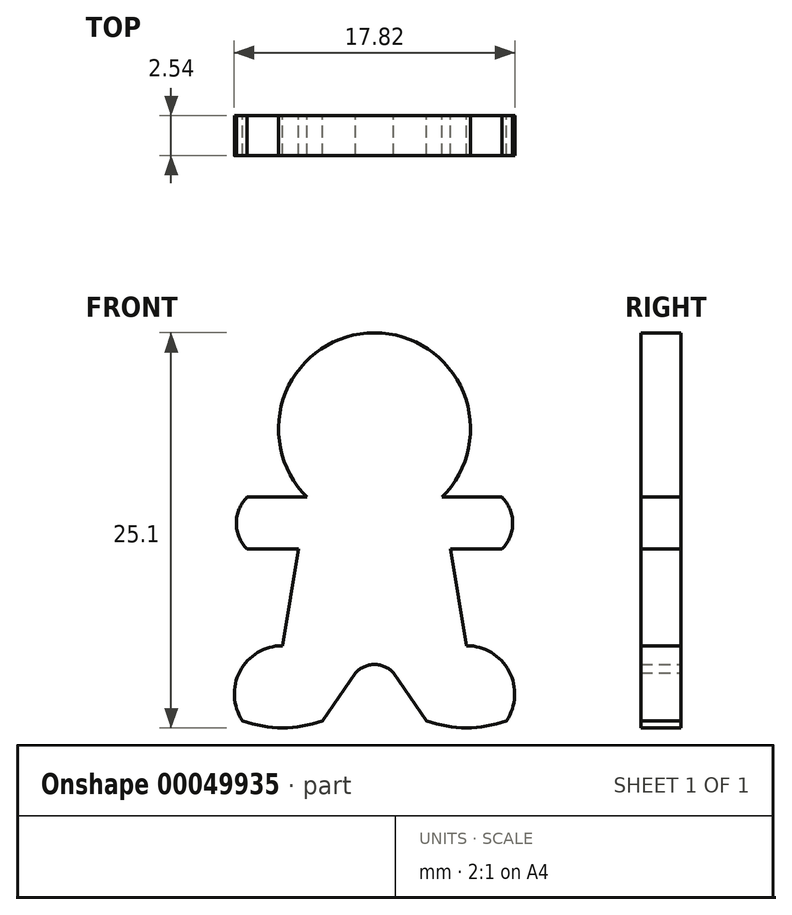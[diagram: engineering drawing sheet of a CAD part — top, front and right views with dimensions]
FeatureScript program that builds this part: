
annotation { "Feature Type Name" : "Feature", "Feature Type Description" : "" }
export const myFeature = defineFeature(function(context is Context, id is Id, definition is map)
    precondition{}
    {
        {
            var Q0;
            Q0=qCreatedBy(makeId("Front.planeOp"),FACE);
            var sketch = newSketch(context, id + "F0", { "sketchPlane" : qUnion([Q0])});
            skCircle(sketch, "E0", {"center": v(0, 0) * mm, "radius": 6.1 * mm});
            skLineSegment(sketch, "E1", {"start": v(6.1, 0) * mm, "end": v(6.1, -6.1) * mm, "construction": true});
            skLineSegment(sketch, "E2", {"start": v(6.1, -6.1) * mm, "end": v(-6.1, -6.1) * mm, "construction": true});
            skLineSegment(sketch, "E3", {"start": v(-6.1, -6.1) * mm, "end": v(-6.1, 6.1) * mm, "construction": true});
            skLineSegment(sketch, "E4", {"start": v(-6.1, 6.1) * mm, "end": v(6.1, 6.1) * mm, "construction": true});
            skLineSegment(sketch, "E5", {"start": v(6.1, 6.1) * mm, "end": v(6.1, 0) * mm, "construction": true});
            skLineSegment(sketch, "E6", {"start": v(0, 0) * mm, "end": v(-3.56, 0) * mm});
            skPoint(sketch, "E6.endSnap0", {"position": v(-6.1, 0) * mm});
            skLineSegment(sketch, "E7", {"start": v(0, 0) * mm, "end": v(3.56, 0) * mm});
            skLineSegment(sketch, "E8", {"start": v(-6.1, -6.1) * mm, "end": v(-4.57, -6.1) * mm});
            skLineSegment(sketch, "E9", {"start": v(6.1, -6.1) * mm, "end": v(4.57, -6.1) * mm});
            skLineSegment(sketch, "E10", {"start": v(-3.56, 0) * mm, "end": v(-4.57, -6.1) * mm});
            skLineSegment(sketch, "E11", {"start": v(3.56, 0) * mm, "end": v(4.57, -6.1) * mm});
            skLineSegment(sketch, "E12", {"start": v(3.56, 0) * mm, "end": v(5.85, -13.78) * mm});
            skLineSegment(sketch, "E13", {"start": v(-3.56, 0) * mm, "end": v(-5.85, -13.78) * mm});
            skLineSegment(sketch, "E14", {"start": v(-5.85, -13.78) * mm, "end": v(5.85, -13.78) * mm});
            skLineSegment(sketch, "E15", {"start": v(4.28, -4.34) * mm, "end": v(8.09, -4.34) * mm});
            skLineSegment(sketch, "E16", {"start": v(-4.28, -4.34) * mm, "end": v(-8.09, -4.34) * mm});
            skLineSegment(sketch, "E17", {"start": v(-4.28, -4.34) * mm, "end": v(-4.28, -7.64) * mm, "construction": true});
            skLineSegment(sketch, "E18", {"start": v(4.28, -4.34) * mm, "end": v(4.28, -7.64) * mm, "construction": true});
            skLineSegment(sketch, "E19", {"start": v(-4.28, -7.64) * mm, "end": v(-8.09, -7.64) * mm});
            skLineSegment(sketch, "E20", {"start": v(4.28, -7.64) * mm, "end": v(8.09, -7.64) * mm});
            skLineSegment(sketch, "E21", {"start": v(-8.09, -4.34) * mm, "end": v(-8.09, -7.64) * mm, "construction": true});
            skLineSegment(sketch, "E22", {"start": v(8.09, -4.34) * mm, "end": v(8.09, -7.64) * mm, "construction": true});
            skLineSegment(sketch, "E23", {"start": v(8.09, -6) * mm, "end": v(8.78, -6) * mm, "construction": true});
            skLineSegment(sketch, "E24", {"start": v(-8.09, -6) * mm, "end": v(-8.78, -6) * mm, "construction": true});
            skArc(sketch, "E25", {"start": v(-8.09, -4.34) * mm, "mid": v(-8.78, -6) * mm, "end": v(-8.09, -7.64) * mm});
            skArc(sketch, "E26", {"start": v(8.09, -7.64) * mm, "mid": v(8.78, -6) * mm, "end": v(8.09, -4.34) * mm});
            skLineSegment(sketch, "E27", {"start": v(0, 0) * mm, "end": v(0, -18.54) * mm, "construction": true});
            skLineSegment(sketch, "E28", {"start": v(0, -18.54) * mm, "end": v(-3.3, -18.54) * mm, "construction": true});
            skLineSegment(sketch, "E29", {"start": v(0, -18.54) * mm, "end": v(3.3, -18.54) * mm, "construction": true});
            skLineSegment(sketch, "E30", {"start": v(0, -13.78) * mm, "end": v(-3.3, -18.54) * mm});
            skLineSegment(sketch, "E31", {"start": v(0, -13.78) * mm, "end": v(3.3, -18.54) * mm});
            skLineSegment(sketch, "E32", {"start": v(3.3, -18.54) * mm, "end": v(8.38, -18.54) * mm});
            skLineSegment(sketch, "E33", {"start": v(-3.3, -18.54) * mm, "end": v(-8.38, -18.54) * mm});
            skArc(sketch, "E34", {"start": v(-5.85, -13.78) * mm, "mid": v(-8.55, -15.4) * mm, "end": v(-8.38, -18.54) * mm});
            skArc(sketch, "E35", {"start": v(8.38, -18.54) * mm, "mid": v(8.55, -15.4) * mm, "end": v(5.85, -13.78) * mm});
            skLineSegment(sketch, "E36", {"start": v(-1.2, -15.5) * mm, "end": v(1.2, -15.5) * mm, "construction": true});
            skArc(sketch, "E37", {"start": v(1.2, -15.5) * mm, "mid": v(0, -14.97) * mm, "end": v(-1.2, -15.5) * mm});
            skLineSegment(sketch, "E38", {"start": v(-5.84, -18.54) * mm, "end": v(-5.84, -19) * mm});
            skLineSegment(sketch, "E39", {"start": v(5.84, -18.54) * mm, "end": v(5.84, -19) * mm});
            skArc(sketch, "E40", {"start": v(-8.38, -18.54) * mm, "mid": v(-5.84, -19) * mm, "end": v(-3.3, -18.54) * mm});
            skArc(sketch, "E41", {"start": v(3.3, -18.54) * mm, "mid": v(5.84, -19) * mm, "end": v(8.38, -18.54) * mm});
            skSolve(sketch);
        }
        {
            var Q0;
            Q0 = qSketchRegion(id + "F0", true);
            extrude(context, id + "F1", {"entities" : qUnion([Q0]), "depth" : 2.54 * mm});
        }
    });
